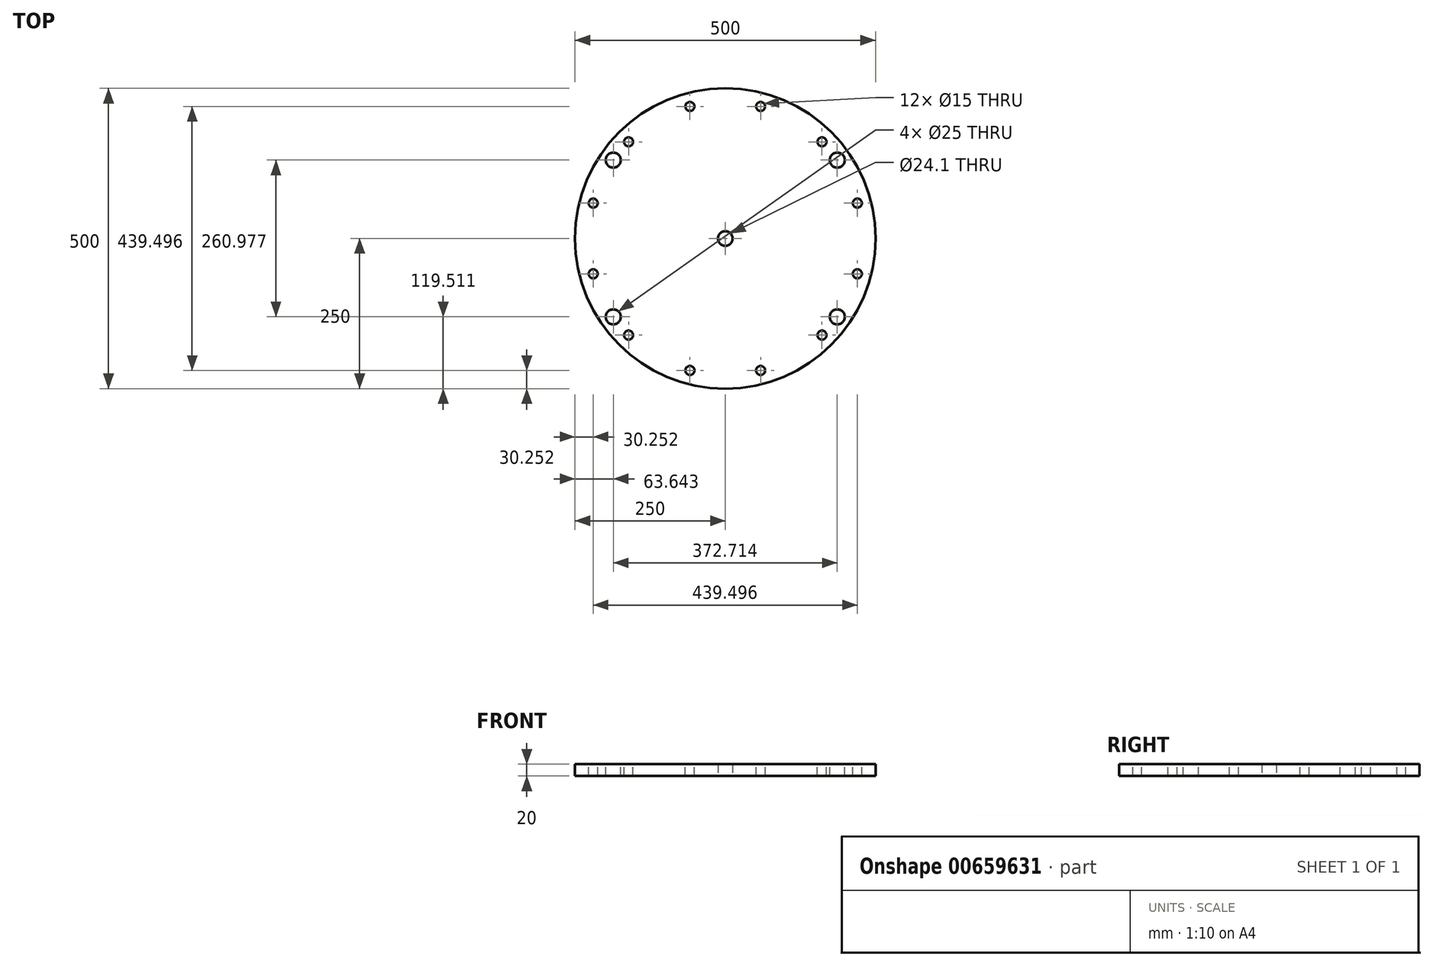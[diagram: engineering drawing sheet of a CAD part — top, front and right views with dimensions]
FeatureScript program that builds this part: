
annotation { "Feature Type Name" : "Feature", "Feature Type Description" : "" }
export const myFeature = defineFeature(function(context is Context, id is Id, definition is map)
    precondition{}
    {
        {
            var Q0;
            Q0=qCreatedBy(makeId("Top.planeOp"),FACE);
            var sketch = newSketch(context, id + "F0", { "sketchPlane" : qUnion([Q0])});
            skCircle(sketch, "E0", {"center": v(0, 0) * mm, "radius": 12.05 * mm});
            skCircle(sketch, "E1", {"center": v(0, 0) * mm, "radius": 250 * mm});
            skSolve(sketch);
        }
        {
            var Q0;
            Q0=qSketchRegion(id+"F0",true);
            extrude(context, id + "F1", {"entities" : qUnion([Q0]), "depth" : 20 * mm, "offsetDistance" : 25 * mm});
        }
        {
            var Q0;
            Q0=makeQuery(id+"FyJSGKeDKdkLdRm_1.boolean.opBoolean","MERGE",FACE,{"derivedFrom":[makeQuery(id+"F1.opExtrude","CAP_FACE",FACE,{"disambiguationData":[OSD([sQuery(id+"F0.wireOp",EDGE,"xTTwQilN-fKaz-kDPW-e2K0-96Pd5emqFTFM"),sQuery(id+"F0.wireOp",EDGE,"E0")])],"isStart":false}),makeQuery(id+"FyJSGKeDKdkLdRm_1.opRevolve","SWEPT_FACE",FACE,{"disambiguationData":[OSD([sQuery(id+"FfHtCZrtJ99MtFh_1.wireOp",EDGE,"ooufrKQF-JUJc-YrDT-QNZE-3XqY6eCNmfmj")])]})]});
            var sketch = newSketch(context, id + "F2", { "sketchPlane" : qUnion([Q0])});
            skCircle(sketch, "E2", {"center": v(219.75, 58.88) * mm, "radius": 7.5 * mm});
            skLineSegment(sketch, "E3", {"start": v(219.75, 58.88) * mm, "end": v(0, 0) * mm, "construction": true});
            skLineSegment(sketch, "E4", {"start": v(0, 0) * mm, "end": v(54.06, 0) * mm, "construction": true});
            skLineSegment(sketch, "E5.1.0", {"start": v(160.87, 160.87) * mm, "end": v(0, 0) * mm, "construction": true});
            skCircle(sketch, "E5.1.1", {"center": v(160.87, 160.87) * mm, "radius": 7.5 * mm});
            skLineSegment(sketch, "E5.2.0", {"start": v(58.88, 219.75) * mm, "end": v(0, 0) * mm, "construction": true});
            skCircle(sketch, "E5.2.1", {"center": v(58.88, 219.75) * mm, "radius": 7.5 * mm});
            skLineSegment(sketch, "E5.3.0", {"start": v(-58.88, 219.75) * mm, "end": v(0, 0) * mm, "construction": true});
            skCircle(sketch, "E5.3.1", {"center": v(-58.88, 219.75) * mm, "radius": 7.5 * mm});
            skLineSegment(sketch, "E5.4.0", {"start": v(-160.87, 160.87) * mm, "end": v(0, 0) * mm, "construction": true});
            skCircle(sketch, "E5.4.1", {"center": v(-160.87, 160.87) * mm, "radius": 7.5 * mm});
            skLineSegment(sketch, "E5.5.0", {"start": v(-219.75, 58.88) * mm, "end": v(0, 0) * mm, "construction": true});
            skCircle(sketch, "E5.5.1", {"center": v(-219.75, 58.88) * mm, "radius": 7.5 * mm});
            skLineSegment(sketch, "E5.6.0", {"start": v(-219.75, -58.88) * mm, "end": v(0, 0) * mm, "construction": true});
            skCircle(sketch, "E5.6.1", {"center": v(-219.75, -58.88) * mm, "radius": 7.5 * mm});
            skLineSegment(sketch, "E5.7.0", {"start": v(-160.87, -160.87) * mm, "end": v(0, 0) * mm, "construction": true});
            skCircle(sketch, "E5.7.1", {"center": v(-160.87, -160.87) * mm, "radius": 7.5 * mm});
            skLineSegment(sketch, "E5.8.0", {"start": v(-58.88, -219.75) * mm, "end": v(0, 0) * mm, "construction": true});
            skCircle(sketch, "E5.8.1", {"center": v(-58.88, -219.75) * mm, "radius": 7.5 * mm});
            skLineSegment(sketch, "E5.9.0", {"start": v(58.88, -219.75) * mm, "end": v(0, 0) * mm, "construction": true});
            skCircle(sketch, "E5.9.1", {"center": v(58.88, -219.75) * mm, "radius": 7.5 * mm});
            skLineSegment(sketch, "E5.10.0", {"start": v(160.87, -160.87) * mm, "end": v(0, 0) * mm, "construction": true});
            skCircle(sketch, "E5.10.1", {"center": v(160.87, -160.87) * mm, "radius": 7.5 * mm});
            skLineSegment(sketch, "E5.11.0", {"start": v(219.75, -58.88) * mm, "end": v(0, 0) * mm, "construction": true});
            skCircle(sketch, "E5.11.1", {"center": v(219.75, -58.88) * mm, "radius": 7.5 * mm});
            skPoint(sketch, "E5.center", {"position": v(0, 0) * mm});
            skSolve(sketch);
        }
        {
            var Q0;
            Q0=qSketchRegion(id+"F2",true);
            extrude(context, id + "F3", {"entities" : qUnion([Q0]), "operationType" : NewBodyOperationType.REMOVE, "endBound" : BoundingType.UP_TO_NEXT, "oppositeDirection" : true, "depth" : 25 * mm, "offsetDistance" : 25 * mm});
        }
        {
            var Q0;
            Q0=makeQuery(id+"FyJSGKeDKdkLdRm_1.boolean.opBoolean","MERGE",FACE,{"derivedFrom":[makeQuery(id+"F1.opExtrude","CAP_FACE",FACE,{"disambiguationData":[OSD([sQuery(id+"F0.wireOp",EDGE,"E0"),sQuery(id+"F0.wireOp",EDGE,"E1")])],"isStart":false}),makeQuery(id+"FyJSGKeDKdkLdRm_1.opRevolve","SWEPT_FACE",FACE,{"disambiguationData":[OSD([sQuery(id+"FfHtCZrtJ99MtFh_1.wireOp",EDGE,"ooufrKQF-JUJc-YrDT-QNZE-3XqY6eCNmfmj")])]})]});
            var sketch = newSketch(context, id + "F4", { "sketchPlane" : qUnion([Q0])});
            skCircle(sketch, "E6", {"center": v(186.36, 130.49) * mm, "radius": 12.5 * mm});
            skPoint(sketch, "E7.center", {"position": v(0, 0) * mm});
            skLineSegment(sketch, "E8", {"start": v(186.36, 130.49) * mm, "end": v(0, 0) * mm, "construction": true});
            skLineSegment(sketch, "E9", {"start": v(0, 0) * mm, "end": v(57.44, 0) * mm, "construction": true});
            skLineSegment(sketch, "E10.MirrorCS", {"start": v(-186.36, 130.49) * mm, "end": v(0, 0) * mm, "construction": true});
            skCircle(sketch, "E11.MirrorC", {"center": v(-186.36, 130.49) * mm, "radius": 12.5 * mm});
            skCircle(sketch, "E12.MirrorC", {"center": v(-186.36, -130.49) * mm, "radius": 12.5 * mm});
            skCircle(sketch, "E13.MirrorC", {"center": v(186.36, -130.49) * mm, "radius": 12.5 * mm});
            skLineSegment(sketch, "E14.MirrorCS", {"start": v(186.36, -130.49) * mm, "end": v(0, 0) * mm, "construction": true});
            skSolve(sketch);
        }
        {
            var Q0;
            Q0=qSketchRegion(id+"F4",true);
            extrude(context, id + "F5", {"entities" : qUnion([Q0]), "operationType" : NewBodyOperationType.REMOVE, "oppositeDirection" : true, "depth" : 20 * mm, "offsetDistance" : 25 * mm});
        }
    });
